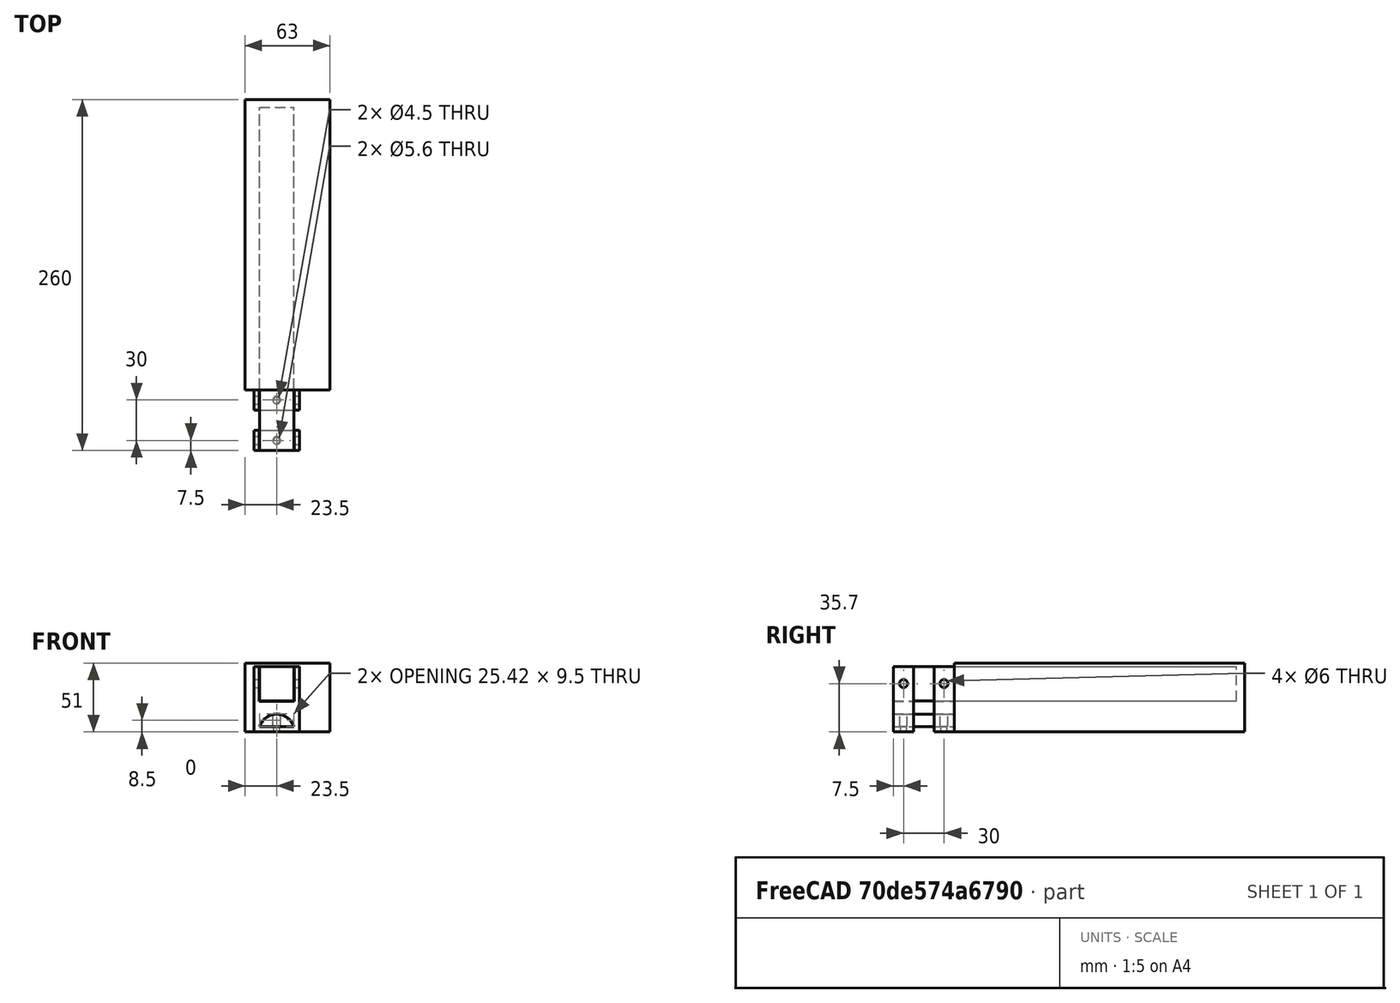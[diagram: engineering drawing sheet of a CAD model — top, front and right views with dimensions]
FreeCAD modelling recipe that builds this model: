
FCSTD DOCUMENT  (FreeCAD 0.19R24276 (Git))
Label: outerLook04132022
License: All rights reserved
LicenseURL: http://en.wikipedia.org/wiki/All_rights_reserved
objects: Part::Cut×13, Part::Box×12, Part::Cylinder×9, Part::MultiFuse×1
note: 35 computed .brp shape members not serialized (recipe doc carries the construction recipe); baked Part::Feature solids carry a one-line shape summary decoded from their .brp

FEATURE [Part::Box] Box012  label="Shell_Holder001"
  AttacherType = Attacher::AttachEngine3D
  Height = 20
  Length = 27
  Placement = pos=(0,0,27) rot=(0,0,1;0rad)
  Width = 200
FEATURE [Part::Cylinder] Cylinder
  Angle = 360
  AttacherType = Attacher::AttachEngine3D
  Height = 120
  Placement = pos=(13.5,15,43) rot=(-1,0,0;1.5708rad)
  Radius = 13
FEATURE [Part::Cut] Cut005  label="Shell_Holder"
  Base = -> Cylinder
  Placement = pos=(0,-15,0) rot=(0,0,1;0rad)
  Tool = -> Box012
FEATURE [Part::Box] Box  label="TSlotFrameCut"
  AttacherType = Attacher::AttachEngine3D
  Height = 26
  Length = 26
  Placement = pos=(0.5,0,65.7) rot=(0,0,1;0rad)
  Width = 254
FEATURE [Part::Box] Box013  label="TSlotFrame001"
  AttacherType = Attacher::AttachEngine3D
  Height = 25.4
  Length = 25.4
  Placement = pos=(0.8,0,66) rot=(0,0,1;0rad)
  Width = 254
FEATURE [Part::Box] Box014  label="TSlotMount"
  AttacherType = Attacher::AttachEngine3D
  Height = 48.4
  Length = 33.4
  Placement = pos=(-3.2,0,43) rot=(0,0,1;0rad)
  Width = 15
FEATURE [Part::Box] Box015  label="TSlotMount001"
  AttacherType = Attacher::AttachEngine3D
  Height = 48.4
  Length = 33.4
  Placement = pos=(-3.2,30,43) rot=(0,0,1;0rad)
  Width = 15
FEATURE [Part::Cylinder] Cylinder008  label="NailMimic002"
  Angle = 360
  AttacherType = Attacher::AttachEngine3D
  Height = 100
  Placement = pos=(-56.4,7.5,78.7) rot=(0,1,0;1.5708rad)
  Radius = 3
FEATURE [Part::Cylinder] Cylinder009  label="NailMimic003"
  Angle = 360
  AttacherType = Attacher::AttachEngine3D
  Height = 100
  Placement = pos=(-56.4,37.5,78.7) rot=(0,1,0;1.5708rad)
  Radius = 3
FEATURE [Part::Cylinder] Cylinder010
  Angle = 360
  AttacherType = Attacher::AttachEngine3D
  Height = 120
  Placement = pos=(13.5,15,43) rot=(-1,0,0;1.5708rad)
  Radius = 13.25
FEATURE [Part::Box] Box016  label="Shell_Holder002"
  AttacherType = Attacher::AttachEngine3D
  Height = 20
  Length = 27
  Placement = pos=(0,0,26.75) rot=(0,0,1;0rad)
  Width = 200
FEATURE [Part::Cut] Cut006  label="ShellCut"
  Base = -> Cylinder010
  Placement = pos=(0,-15,0) rot=(0,0,1;0rad)
  Tool = -> Box016
FEATURE [Part::Cylinder] Cylinder011
  Angle = 360
  AttacherType = Attacher::AttachEngine3D
  Height = 10
  Placement = pos=(13.5,7.5,47) rot=(0,0,1;1.5708rad)
  Radius = 2.8
FEATURE [Part::Cylinder] Cylinder012
  Angle = 360
  AttacherType = Attacher::AttachEngine3D
  Height = 10
  Placement = pos=(13.5,37.5,47) rot=(0,0,1;1.5708rad)
  Radius = 2.8
FEATURE [Part::Box] Box017  label="ShellCuts"
  AttacherType = Attacher::AttachEngine3D
  Height = 51
  Length = 63
  Placement = pos=(-10,45,43) rot=(0,0,1;0rad)
  Width = 215
FEATURE [Part::Box] Box018  label="TSlotFrameCut001"
  AttacherType = Attacher::AttachEngine3D
  Height = 26
  Length = 26
  Placement = pos=(0.5,0,65.7) rot=(0,0,1;0rad)
  Width = 254
FEATURE [Part::Box] Box020  label="ShellCuts001"
  AttacherType = Attacher::AttachEngine3D
  Height = 51
  Length = 63
  Placement = pos=(-10,45,43) rot=(0,0,1;0rad)
  Width = 215
FEATURE [Part::Box] Box021  label="ShellCuts002"
  AttacherType = Attacher::AttachEngine3D
  Height = 51
  Length = 63
  Placement = pos=(-10,45,43) rot=(0,0,1;0rad)
  Width = 215
FEATURE [Part::Box] Box022  label="ShellCuts003"
  AttacherType = Attacher::AttachEngine3D
  Height = 51
  Length = 63
  Placement = pos=(-10,45,43) rot=(0,0,1;0rad)
  Width = 215
FEATURE [Part::MultiFuse] Fusion  label="ShellCuts004"
  Shapes = -> [Cylinder012,Cylinder011]
FEATURE [Part::Cut] Cut  label="Shell"
  Base = -> Cut005
  Tool = -> Box020
FEATURE [Part::Cut] Cut007  label="Shell001"
  Base = -> Cut
  Tool = -> Fusion
FEATURE [Part::Cut] Cut008  label="TSlotMount003"
  Base = -> Box014
  Tool = -> Box
FEATURE [Part::Cut] Cut009  label="TSlotMount002"
  Base = -> Box015
  Tool = -> Box018
FEATURE [Part::Cylinder] Cylinder013
  Angle = 360
  AttacherType = Attacher::AttachEngine3D
  Height = 120
  Placement = pos=(13.5,15,43) rot=(-1,0,0;1.5708rad)
  Radius = 13.25
FEATURE [Part::Box] Box023  label="Shell_Holder003"
  AttacherType = Attacher::AttachEngine3D
  Height = 20
  Length = 27
  Placement = pos=(0,0,26.75) rot=(0,0,1;0rad)
  Width = 200
FEATURE [Part::Cut] Cut010  label="ShellCut001"
  Base = -> Cylinder013
  Placement = pos=(0,-15,0) rot=(0,0,1;0rad)
  Tool = -> Box023
FEATURE [Part::Cut] Cut011  label="TSlotMount004"
  Base = -> Cut009
  Tool = -> Cut006
FEATURE [Part::Cut] Cut012  label="TSlotMount005"
  Base = -> Cut008
  Tool = -> Cut010
FEATURE [Part::Cut] Cut013  label="TSlotMount006"
  Base = -> Cut011
  Tool = -> Cylinder009
FEATURE [Part::Cut] Cut014  label="TSlotMount007"
  Base = -> Cut012
  Tool = -> Cylinder008
FEATURE [Part::Cylinder] Cylinder014
  Angle = 360
  AttacherType = Attacher::AttachEngine3D
  Height = 10
  Placement = pos=(13.5,7.5,43) rot=(0,0,1;0rad)
  Radius = 2.25
FEATURE [Part::Cylinder] Cylinder015
  Angle = 360
  AttacherType = Attacher::AttachEngine3D
  Height = 10
  Placement = pos=(13.5,37.5,43) rot=(0,0,1;0rad)
  Radius = 2.25
FEATURE [Part::Cut] Cut015  label="TSlotMount008"
  Base = -> Cut014
  Tool = -> Cylinder014
FEATURE [Part::Cut] Cut016  label="TSlotMount009"
  Base = -> Cut013
  Tool = -> Cylinder015
